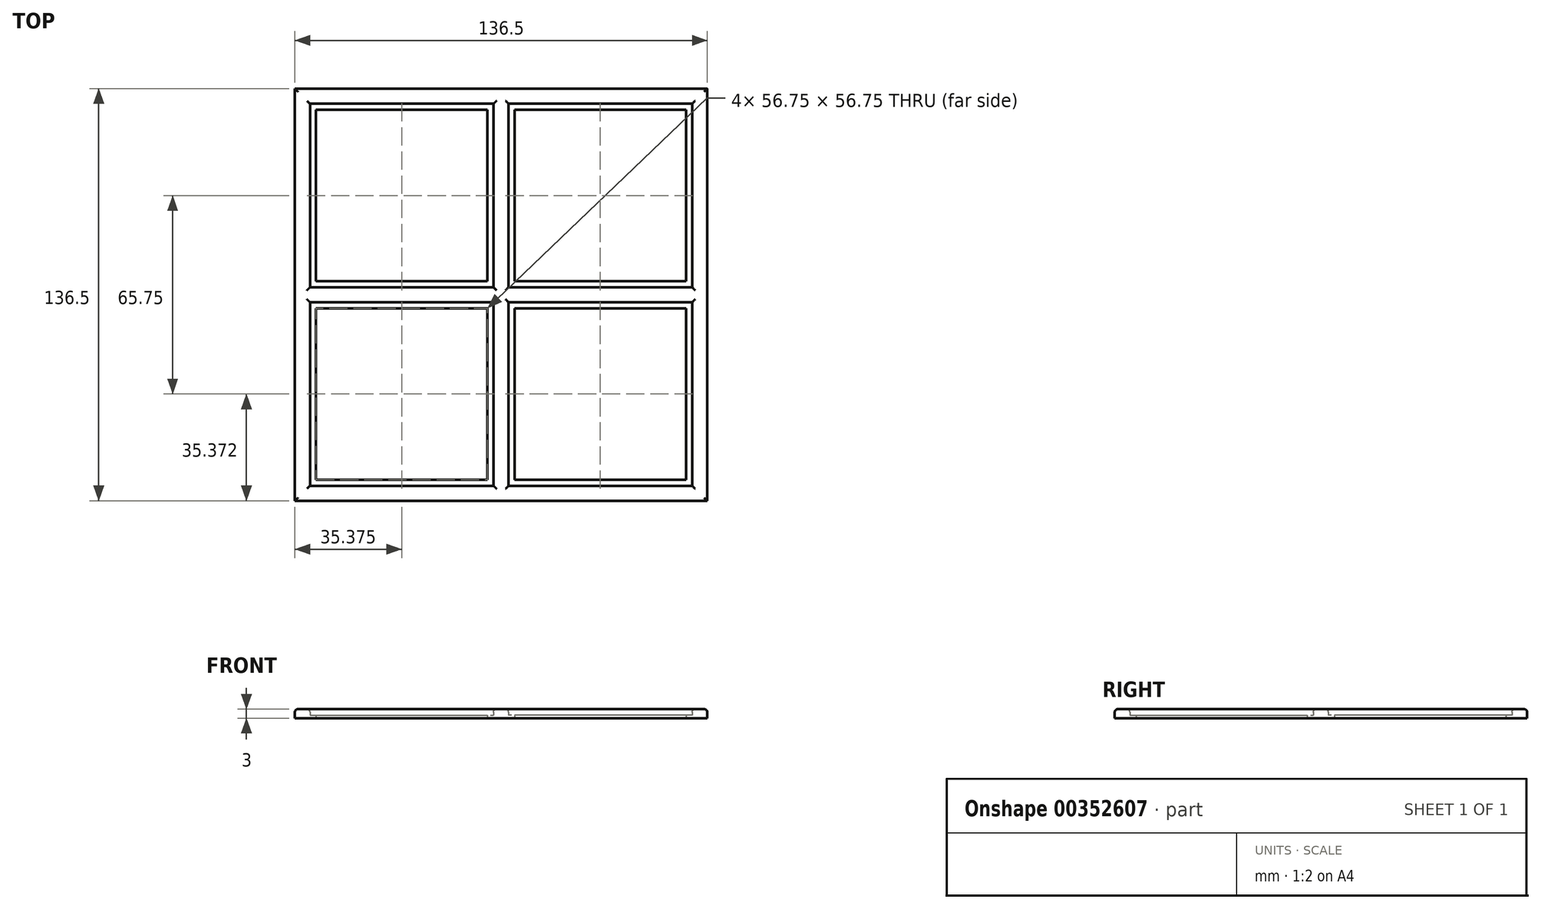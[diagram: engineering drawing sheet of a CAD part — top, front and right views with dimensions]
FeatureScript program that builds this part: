
annotation { "Feature Type Name" : "Feature", "Feature Type Description" : "" }
export const myFeature = defineFeature(function(context is Context, id is Id, definition is map)
    precondition{}
    {
        {
            var Q0;
            Q0=qCreatedBy(makeId("Top.planeOp"),FACE);
            var sketch = newSketch(context, id + "F0", { "sketchPlane" : qUnion([Q0])});
            skLineSegment(sketch, "E0.bottom", {"start": v(-63.25, 26.55) * mm, "end": v(-2.5, 26.55) * mm});
            skLineSegment(sketch, "E0.top", {"start": v(-63.25, -34.2) * mm, "end": v(-2.5, -34.2) * mm});
            skLineSegment(sketch, "E0.left", {"start": v(-63.25, 26.55) * mm, "end": v(-63.25, -34.2) * mm});
            skLineSegment(sketch, "E0.right", {"start": v(-2.5, 26.55) * mm, "end": v(-2.5, -34.2) * mm});
            skPoint(sketch, "E1", {"position": v(-2.5, 26.55) * mm});
            skPoint(sketch, "E2", {"position": v(-2.5, 31.55) * mm});
            skPoint(sketch, "E3", {"position": v(-2.5, -34.2) * mm});
            skPoint(sketch, "E4", {"position": v(-2.5, -36.7) * mm});
            skPoint(sketch, "E5", {"position": v(-63.25, -36.7) * mm});
            skPoint(sketch, "E6", {"position": v(-63.25, 31.55) * mm});
            skPoint(sketch, "E7", {"position": v(-63.25, 26.55) * mm});
            skPoint(sketch, "E8", {"position": v(-68.25, 26.55) * mm});
            skPoint(sketch, "E9", {"position": v(-68.25, 31.55) * mm});
            skPoint(sketch, "E10", {"position": v(0, -36.7) * mm});
            skLineSegment(sketch, "E11.bottom", {"start": v(-68.25, 31.55) * mm, "end": v(0, 31.55) * mm});
            skLineSegment(sketch, "E11.top", {"start": v(-68.25, -36.7) * mm, "end": v(0, -36.7) * mm});
            skLineSegment(sketch, "E11.left", {"start": v(-68.25, 31.55) * mm, "end": v(-68.25, -36.7) * mm});
            skLineSegment(sketch, "E11.right", {"start": v(0, 31.55) * mm, "end": v(0, -36.7) * mm});
            skPoint(sketch, "E12", {"position": v(-34.12, 31.55) * mm});
            skPoint(sketch, "E13", {"position": v(-34.12, 41.55) * mm});
            skLineSegment(sketch, "E14", {"start": v(-34.12, 41.55) * mm, "end": v(-34.12, 31.55) * mm});
            skPoint(sketch, "E15", {"position": v(-34.12, 36.55) * mm});
            skPoint(sketch, "E16", {"position": v(-34.12, 38.98) * mm});
            skPoint(sketch, "E17", {"position": v(-61.25, 26.55) * mm});
            skPoint(sketch, "E18", {"position": v(-63.25, 24.55) * mm});
            skPoint(sketch, "E19", {"position": v(-61.25, 24.55) * mm});
            skPoint(sketch, "E20", {"position": v(-2.5, -32.2) * mm});
            skPoint(sketch, "E21", {"position": v(-4.5, -34.2) * mm});
            skPoint(sketch, "E22", {"position": v(-4.5, -32.2) * mm});
            skLineSegment(sketch, "E23.bottom", {"start": v(-61.25, 24.55) * mm, "end": v(-4.5, 24.55) * mm});
            skLineSegment(sketch, "E23.top", {"start": v(-61.25, -32.2) * mm, "end": v(-4.5, -32.2) * mm});
            skLineSegment(sketch, "E23.left", {"start": v(-61.25, 24.55) * mm, "end": v(-61.25, -32.2) * mm});
            skLineSegment(sketch, "E23.right", {"start": v(-4.5, 24.55) * mm, "end": v(-4.5, -32.2) * mm});
            skLineSegment(sketch, "E24", {"start": v(0, 31.55) * mm, "end": v(0, 41.55) * mm});
            skPoint(sketch, "E25", {"position": v(0, 38.98) * mm});
            skCircle(sketch, "E26", {"center": v(0, 31.55) * mm, "radius": 10 * mm});
            skCircle(sketch, "E27", {"center": v(0, 31.55) * mm, "radius": 7.43 * mm});
            skLineSegment(sketch, "E28", {"start": v(7.43, 31.55) * mm, "end": v(10, 31.55) * mm});
            skLineSegment(sketch, "E29", {"start": v(5.5, 26.55) * mm, "end": v(8.66, 26.55) * mm});
            skSolve(sketch);
        }
        {
            var Q0;
            Q0=makeQuery(id+"F0.imprint","IMPRINT",FACE,{"disambiguationData":[TD([[makeQuery(id+"F0.imprint","IMPRINT",EDGE,{"derivedFrom":sQuery(id+"F0.wireOp",EDGE,"E0.top")}),-1.0]])]});
            var Q1;
            {var subQ0=sQuery(id+"F0.wireOp",EDGE,"323iFSkM-69Tl-kqoX-bfbl-zxdwPlZIsCMZ");var subQ1=sQuery(id+"F0.wireOp",EDGE,"E0.bottom");var subQ2=makeQuery(id+"F0.imprint","INTERSECT",VERTEX,{"disambiguationData":[OD(0.0)],"derivedFrom":[subQ1,subQ0]});Q1=makeQuery(id+"F0.imprint","IMPRINT",FACE,{"disambiguationData":[TD([[makeQuery(id+"F0.imprint","IMPRINT",EDGE,{"disambiguationData":[TD([[subQ2,-1.0]])],"derivedFrom":subQ1}),1.0]])]});}
            var Q2;
            {var subQ0=sQuery(id+"F0.wireOp",EDGE,"S2f47POQ-odG1-F0nU-moLb-DiT50xx8mqJj");var subQ1=sQuery(id+"F0.wireOp",EDGE,"E0.bottom");var subQ2=makeQuery(id+"F0.imprint","INTERSECT",VERTEX,{"disambiguationData":[OD(1.0)],"derivedFrom":[subQ1,subQ0]});Q2=makeQuery(id+"F0.imprint","IMPRINT",FACE,{"disambiguationData":[TD([[makeQuery(id+"F0.imprint","IMPRINT",EDGE,{"disambiguationData":[TD([[subQ2,-1.0]])],"derivedFrom":subQ1}),1.0]])]});}
            var Q3;
            {var subQ0=sQuery(id+"F0.wireOp",EDGE,"S2f47POQ-odG1-F0nU-moLb-DiT50xx8mqJj");var subQ1=sQuery(id+"F0.wireOp",EDGE,"E0.bottom");var subQ2=makeQuery(id+"F0.imprint","INTERSECT",VERTEX,{"disambiguationData":[OD(0.0)],"derivedFrom":[subQ1,subQ0]});Q3=makeQuery(id+"F0.imprint","IMPRINT",FACE,{"disambiguationData":[TD([[makeQuery(id+"F0.imprint","IMPRINT",EDGE,{"disambiguationData":[TD([[subQ2,-1.0]])],"derivedFrom":subQ1}),1.0]])]});}
            var Q4;
            {var subQ0=sQuery(id+"F0.wireOp",EDGE,"E27");var subQ1=sQuery(id+"F0.wireOp",EDGE,"E0.right");var subQ2=makeQuery(id+"F0.imprint","INTERSECT",VERTEX,{"derivedFrom":[subQ1,subQ0]});Q4=makeQuery(id+"F0.imprint","IMPRINT",FACE,{"disambiguationData":[TD([[makeQuery(id+"F0.imprint","IMPRINT",EDGE,{"disambiguationData":[TD([[subQ2,-1.0]])],"derivedFrom":subQ1}),1.0]])]});}
            var Q5;
            {var subQ6=sQuery(id+"F0.wireOp",EDGE,"E0.bottom");var subQ8=sQuery(id+"F0.wireOp",EDGE,"E0.right");var subQ9=makeQuery(id+"F0.imprint","INTERSECT",VERTEX,{"derivedFrom":[subQ6,subQ8]});Q5=makeQuery(id+"F0.imprint","IMPRINT",FACE,{"disambiguationData":[TD([[makeQuery(id+"F0.imprint","IMPRINT",EDGE,{"disambiguationData":[TD([[subQ9,1.0]])],"derivedFrom":subQ6}),1.0]])]});}
            extrude(context, id + "F1", {"entities" : qUnion([Q0, Q1, Q2, Q3, Q4, Q5]), "depth" : 3 * mm});
        }
        {
            var Q0;
            {var subQ0=sQuery(id+"F0.wireOp",EDGE,"S2f47POQ-odG1-F0nU-moLb-DiT50xx8mqJj");var subQ1=sQuery(id+"F0.wireOp",EDGE,"E0.bottom");var subQ2=makeQuery(id+"F0.imprint","INTERSECT",VERTEX,{"disambiguationData":[OD(0.0)],"derivedFrom":[subQ1,subQ0]});Q0=makeQuery(id+"F0.imprint","IMPRINT",FACE,{"disambiguationData":[TD([[makeQuery(id+"F0.imprint","IMPRINT",EDGE,{"disambiguationData":[TD([[subQ2,-1.0]])],"derivedFrom":subQ1}),-1.0]])]});}
            var Q1;
            {var subQ0=sQuery(id+"F0.wireOp",EDGE,"323iFSkM-69Tl-kqoX-bfbl-zxdwPlZIsCMZ");var subQ1=sQuery(id+"F0.wireOp",EDGE,"E0.bottom");var subQ2=makeQuery(id+"F0.imprint","INTERSECT",VERTEX,{"disambiguationData":[OD(0.0)],"derivedFrom":[subQ1,subQ0]});Q1=makeQuery(id+"F0.imprint","IMPRINT",FACE,{"disambiguationData":[TD([[makeQuery(id+"F0.imprint","IMPRINT",EDGE,{"disambiguationData":[TD([[subQ2,-1.0]])],"derivedFrom":subQ1}),-1.0]])]});}
            var Q2;
            {var subQ0=sQuery(id+"F0.wireOp",EDGE,"S2f47POQ-odG1-F0nU-moLb-DiT50xx8mqJj");var subQ1=sQuery(id+"F0.wireOp",EDGE,"E0.bottom");var subQ2=makeQuery(id+"F0.imprint","INTERSECT",VERTEX,{"disambiguationData":[OD(1.0)],"derivedFrom":[subQ1,subQ0]});Q2=makeQuery(id+"F0.imprint","IMPRINT",FACE,{"disambiguationData":[TD([[makeQuery(id+"F0.imprint","IMPRINT",EDGE,{"disambiguationData":[TD([[subQ2,-1.0]])],"derivedFrom":subQ1}),-1.0]])]});}
            var Q3;
            Q3=makeQuery(id+"F0.imprint","IMPRINT",FACE,{"disambiguationData":[TD([[makeQuery(id+"F0.imprint","IMPRINT",EDGE,{"derivedFrom":sQuery(id+"F0.wireOp",EDGE,"E0.top")}),1.0]])]});
            var Q4;
            {var subQ3=sQuery(id+"F0.wireOp",EDGE,"E26");var subQ10=sQuery(id+"F0.wireOp",EDGE,"E0.bottom");var subQ11=makeQuery(id+"F0.imprint","INTERSECT",VERTEX,{"derivedFrom":[subQ10,subQ3]});Q4=makeQuery(id+"F0.imprint","IMPRINT",FACE,{"disambiguationData":[TD([[makeQuery(id+"F0.imprint","IMPRINT",EDGE,{"disambiguationData":[TD([[subQ11,-1.0]])],"derivedFrom":subQ10}),-1.0]])]});}
            extrude(context, id + "F2", {"entities" : qUnion([Q0, Q1, Q2, Q3, Q4]), "operationType" : NewBodyOperationType.ADD, "depth" : 1 * mm});
        }
        {
            var Q0;
            Q0=makeQuery(id+"F1.opExtrude","CAP_EDGE",EDGE,{"disambiguationData":[OSD([sQuery(id+"F0.wireOp",EDGE,"E0.bottom")])],"isStart":false});
            var Q1;
            Q1=makeQuery(id+"F1.opExtrude","CAP_EDGE",EDGE,{"disambiguationData":[OSD([sQuery(id+"F0.wireOp",EDGE,"E0.left")])],"isStart":false});
            var Q2;
            Q2=makeQuery(id+"F1.opExtrude","CAP_EDGE",EDGE,{"disambiguationData":[OSD([sQuery(id+"F0.wireOp",EDGE,"E0.top")])],"isStart":false});
            var Q3;
            Q3=makeQuery(id+"F1.opExtrude","CAP_EDGE",EDGE,{"disambiguationData":[OSD([sQuery(id+"F0.wireOp",EDGE,"E0.right")])],"isStart":false});
            var Q4;
            {var subQ0=sQuery(id+"F0.wireOp",EDGE,"E11.bottom");var subQ1=makeQuery(id+"F0.imprint","IMPRINT",VERTEX,{"derivedFrom":subQ0});Q4=makeQuery(id+"F1.opExtrude","CAP_EDGE",EDGE,{"disambiguationData":[OSD([subQ0]),TDD([makeQuery(id+"F0.imprint","IMPRINT",EDGE,{"disambiguationData":[TD([[subQ1,1.0]])],"derivedFrom":subQ0}),makeQuery(id+"F0.imprint","IMPRINT",EDGE,{"disambiguationData":[TD([[subQ1,-1.0]])],"derivedFrom":subQ0})])],"isStart":false});}
            var Q5;
            Q5=makeQuery(id+"F1.opExtrude","CAP_EDGE",EDGE,{"disambiguationData":[OSD([sQuery(id+"F0.wireOp",EDGE,"E11.left")])],"isStart":false});
            var Q6;
            Q6=makeQuery(id+"F1.opExtrude","CAP_EDGE",EDGE,{"disambiguationData":[OSD([sQuery(id+"F0.wireOp",EDGE,"E26")])],"isStart":false});
            var Q7;
            Q7=makeQuery(id+"F1.opExtrude","CAP_EDGE",EDGE,{"disambiguationData":[OSD([sQuery(id+"F0.wireOp",EDGE,"E27")])],"isStart":false});
            var Q8;
            {var subQ0=sQuery(id+"F0.wireOp",EDGE,"E11.bottom");Q8=makeQuery(id+"F1.opExtrude","CAP_EDGE",EDGE,{"disambiguationData":[OSD([subQ0]),TDD([makeQuery(id+"F0.imprint","IMPRINT",EDGE,{"disambiguationData":[TD([[makeQuery(id+"F0.imprint","INTERSECT",VERTEX,{"derivedFrom":[subQ0,sQuery(id+"F0.wireOp",EDGE,"E27")]}),-1.0]])],"derivedFrom":subQ0})])],"isStart":false});}
            fillet(context, id + "F3", {"entities" : qUnion([Q0, Q1, Q2, Q3, Q4, Q5, Q6, Q7, Q8]), "radius" : 1 * mm, "tangentPropagation" : true, "allowEdgeOverflow" : false});
        }
        {
            var Q0;
            Q0=makeQuery(id+"F1.opExtrude","SWEPT_BODY",BODY,{"disambiguationData":[OSD([sQuery(id+"F0.wireOp",EDGE,"E0.bottom"),sQuery(id+"F0.wireOp",EDGE,"E0.top"),sQuery(id+"F0.wireOp",EDGE,"E0.left"),sQuery(id+"F0.wireOp",EDGE,"E0.right"),sQuery(id+"F0.wireOp",EDGE,"E11.bottom"),sQuery(id+"F0.wireOp",EDGE,"E11.top"),sQuery(id+"F0.wireOp",EDGE,"E11.left"),sQuery(id+"F0.wireOp",EDGE,"E11.right"),sQuery(id+"F0.wireOp",EDGE,"323iFSkM-69Tl-kqoX-bfbl-zxdwPlZIsCMZ"),sQuery(id+"F0.wireOp",EDGE,"S2f47POQ-odG1-F0nU-moLb-DiT50xx8mqJj")])]});
            var Q1;
            Q1=qCreatedBy(makeId("Right.planeOp"),FACE);
            mirror(context, id + "F4", {"operationType" : NewBodyOperationType.ADD, "entities" : qUnion([Q0]), "mirrorPlane" : qUnion([Q1])});
        }
        {
            var Q0;
            Q0=makeQuery(id+"F1.opExtrude","SWEPT_BODY",BODY,{"disambiguationData":[OSD([sQuery(id+"F0.wireOp",EDGE,"E0.bottom"),sQuery(id+"F0.wireOp",EDGE,"E0.top"),sQuery(id+"F0.wireOp",EDGE,"E0.left"),sQuery(id+"F0.wireOp",EDGE,"E0.right"),sQuery(id+"F0.wireOp",EDGE,"E11.bottom"),sQuery(id+"F0.wireOp",EDGE,"E11.top"),sQuery(id+"F0.wireOp",EDGE,"E11.left"),sQuery(id+"F0.wireOp",EDGE,"E11.right"),sQuery(id+"F0.wireOp",EDGE,"E24"),sQuery(id+"F0.wireOp",EDGE,"E26"),sQuery(id+"F0.wireOp",EDGE,"E27")])]});
            var Q1;
            {var subQ0=makeQuery(id+"F1.opExtrude","SWEPT_FACE",FACE,{"disambiguationData":[OSD([sQuery(id+"F0.wireOp",EDGE,"E11.top")])]});Q1=makeQuery(id+"F4.boolean.opBoolean","MERGE",FACE,{"derivedFrom":[subQ0,makeQuery(id+"F4.opPattern","COPY",FACE,{"derivedFrom":subQ0,"instanceName":"1"})]});}
            mirror(context, id + "F5", {"operationType" : NewBodyOperationType.ADD, "entities" : qUnion([Q0]), "mirrorPlane" : qUnion([Q1])});
        }
    });
